# Revit family: Sanitary_Mixers_Johnson-Suisse_Living_Assist_Basin_Mixer
name_source: partatom
category: Plumbing Fixtures
revit_build: Autodesk Revit 2015 (Build: 20140606_1530(x64)
units: mm (PartAtom-declared; Revit-internal decimal feet)

## types (1)
- Living Assist Basin Mixer
    BIMobject category = Taps & Mixers
    Brand url = http://www.johnsonsuisse.com.au
    Design country = China
    EAN code = https://9325304001166
    Edition number = 1
    IFC Classification = Sanitary Terminal
    MEP Diameter = 1"
    Manufacturer country = China
    Manufacturer name = Johnson Suisse
    Material main = Chrome
    Material secondary = Brass
    Nominal height = 266 mm  [stored 0.872703 ft]
    Nominal width = 52 mm  [stored 0.170604 ft]
    Product Guid = bb2f6905-91af-4d03-9c3e-fc6cf96d35e8
    Product SKU = JTL122
    Product data url = https://bimobject.com
    Product family = Assist
    Product group = Tapware
    Product url = https://johnsonsuisse.com.au
    QR code = http://bimobject.com
    Technical description = https://johnsonsuisse.com.au
    Type = living_assist_basin_mixer : Default
    UNSPSC Code = 301815
    Uniclass 1.4 Code = L725111
    Uniclass 1.4 Description = Mixer taps
    Uniclass 2015 Code = Pr_40_20_87_98
    Uniclass 2015 Name = Washbasin taps
    Weight Net (Kg) = 1.5

note: [stored X ft] marks values corroborated as IEEE doubles in the binary element streams (Revit-internal decimal feet)

## geometry (parser evidence)
native form markers: Sweep x5
no freeform markers — native parametric forms only
